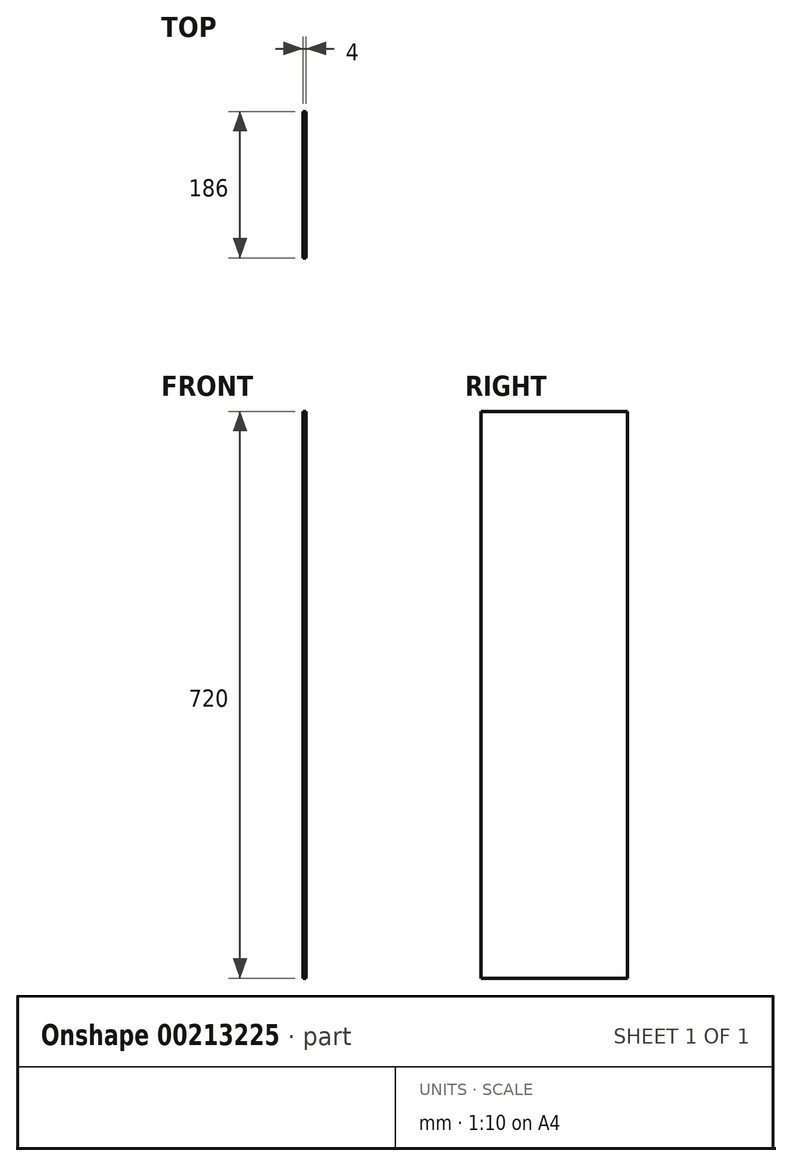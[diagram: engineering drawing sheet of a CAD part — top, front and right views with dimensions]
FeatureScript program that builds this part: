
annotation { "Feature Type Name" : "Feature", "Feature Type Description" : "" }
export const myFeature = defineFeature(function(context is Context, id is Id, definition is map)
    precondition{}
    {
        {
            var Q0;
            Q0=qCreatedBy(makeId("Right.planeOp"),FACE);
            var sketch = newSketch(context, id + "F0", { "sketchPlane" : qUnion([Q0])});
            skLineSegment(sketch, "E0.bottom", {"start": v(93, 360) * mm, "end": v(-93, 360) * mm});
            skLineSegment(sketch, "E0.top", {"start": v(93, -360) * mm, "end": v(-93, -360) * mm});
            skLineSegment(sketch, "E0.left", {"start": v(93, 360) * mm, "end": v(93, -360) * mm});
            skLineSegment(sketch, "E0.right", {"start": v(-93, 360) * mm, "end": v(-93, -360) * mm});
            skPoint(sketch, "E0.middle", {"position": v(0, 0) * mm});
            skSolve(sketch);
        }
        {
            var Q0;
            Q0=makeQuery(id+"F0.imprint","IMPRINT",FACE,{"disambiguationData":[TD([[makeQuery(id+"F0.imprint","IMPRINT",EDGE,{"derivedFrom":sQuery(id+"F0.wireOp",EDGE,"E0.bottom")}),1.0]])]});
            extrude(context, id + "F1", {"entities" : qUnion([Q0]), "endBound" : BoundingType.SYMMETRIC, "depth" : 4 * mm});
        }
    });
